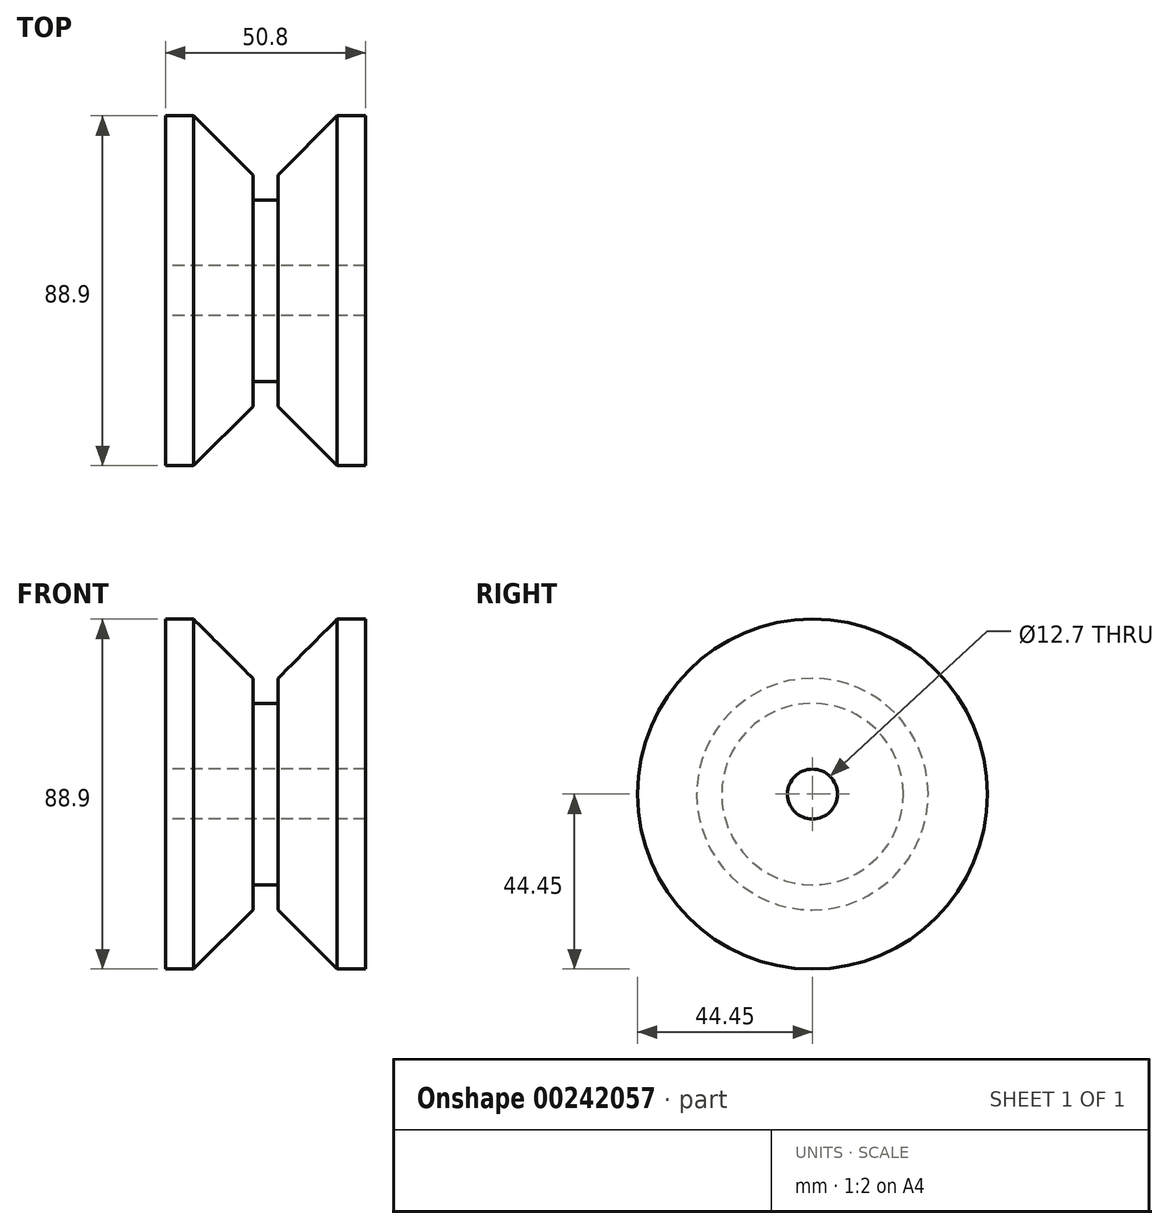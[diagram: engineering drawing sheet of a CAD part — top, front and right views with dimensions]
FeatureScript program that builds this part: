
annotation { "Feature Type Name" : "Feature", "Feature Type Description" : "" }
export const myFeature = defineFeature(function(context is Context, id is Id, definition is map)
    precondition{}
    {
        {
            var Q0;
            Q0=qCreatedBy(makeId("Front.planeOp"),FACE);
            var sketch = newSketch(context, id + "F0", { "sketchPlane" : qUnion([Q0])});
            skLineSegment(sketch, "E0.top", {"start": v(25.4, 44.45) * mm, "end": v(18.22, 44.45) * mm});
            skLineSegment(sketch, "E0.left", {"start": v(25.4, 6.35) * mm, "end": v(25.4, 44.45) * mm});
            skLineSegment(sketch, "E0.right", {"start": v(-25.4, 6.35) * mm, "end": v(-25.4, 44.45) * mm});
            skPoint(sketch, "E0.middle", {"position": v(0, 0) * mm});
            skLineSegment(sketch, "E1.bottom", {"start": v(3.18, 23.06) * mm, "end": v(-3.17, 23.06) * mm});
            skLineSegment(sketch, "E1.left", {"start": v(3.18, 23.06) * mm, "end": v(3.18, 29.4) * mm});
            skLineSegment(sketch, "E1.right", {"start": v(-3.17, 23.06) * mm, "end": v(-3.17, 29.4) * mm});
            skPoint(sketch, "E1.middle", {"position": v(0, 26.23) * mm});
            skLineSegment(sketch, "E2", {"start": v(3.18, 29.4) * mm, "end": v(18.22, 44.45) * mm});
            skLineSegment(sketch, "E3", {"start": v(-3.17, 29.4) * mm, "end": v(-18.22, 44.45) * mm});
            skLineSegment(sketch, "E4.trimOffspring", {"start": v(-18.22, 44.45) * mm, "end": v(-25.4, 44.45) * mm});
            skLineSegment(sketch, "E5", {"start": v(-25.4, 6.35) * mm, "end": v(25.4, 6.35) * mm});
            skPoint(sketch, "E0.bottom.end.orphan", {"position": v(-25.4, -44.45) * mm});
            skPoint(sketch, "E0.bottom.start.orphan", {"position": v(25.4, -44.45) * mm});
            skLineSegment(sketch, "E6", {"start": v(-31.77, 0) * mm, "end": v(31.54, 0) * mm, "construction": true});
            skSolve(sketch);
        }
        {
            var Q0;
            Q0=makeQuery(id+"F0.imprint","IMPRINT",FACE,{"disambiguationData":[TD([[makeQuery(id+"F0.imprint","IMPRINT",EDGE,{"derivedFrom":sQuery(id+"F0.wireOp",EDGE,"E0.top")}),1.0]])]});
            var Q1;
            Q1=sQuery(id+"F0.wireOp",EDGE,"E6");
            revolve(context, id + "F1", {"entities" : qUnion([Q0]), "axis" : qUnion([Q1]), "revolveType" : RevolveType.FULL});
        }
    });
